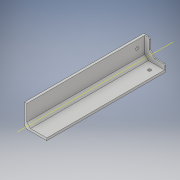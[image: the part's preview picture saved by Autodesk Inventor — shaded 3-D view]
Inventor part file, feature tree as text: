
AUTODESK INVENTOR PART (.ipt)
format: ipt  version: 2018 (Build 220112000, 112)  size: 189,440 bytes
history: native  units: in
note: dims shown in document units (in); Inventor stores cm internally (conversion verified against a paired STEP export)
features: sketch x7, extrude x3, hole x3, plane x1, fillet x1
ambient origin geometry x8: Origin, YZ Plane, XZ Plane, XY Plane, X Axis, Y Axis, Z Axis, Center Point
bodies: Solid1 (feature_tree)
feature tree (15):
  extrude  "Extrusion1"  Depth=0.75in
  extrude  "Extrusion2"  Depth=0.08in
  plane  "Work Plane1"
  extrude  "Extrusion4"  Depth=4.0in TaperAngle=0.0deg
  sketch  "Sketch6"  dims[d11=0.23in d15=0.23in d16=180.0deg]
  hole  "Hole1"  [1 undecoded]
  fillet  "Fillet1"  [1 undecoded]
  hole  "Hole2"  [1 undecoded]
  hole  "Hole3"  [1 undecoded]
  sketch  "Sketch1"  dims[d0=0.75in d1=0.75in]
  sketch  "Sketch2"  dims[d2=0.08in d3=0.08in]
  sketch  "Sketch5"  dims[d8=0.15in d9=4.0in d10=0.0in]
  sketch  "Sketch7"  dims[d18=90.0deg d20=45.0deg]
  sketch  "Sketch8"  dims[d21=0.4in d22=0.04in d23=0.0in]
  sketch  "Sketch9"  dims[d30=0.5in d37=0.05in d38=0.6in d39=180.0deg d40=0.25in d41=0.3in d42=0.25in d43=0.5in d44=0.2in d45=0.0in d46=0.25in d47=0.25in d48=0.75in d49=0.375in d50=0.25in d51=0.5635in d52=1.0in d53=0.8108in d54=0.05in d55=0.25in d56=0.3in d57=0.1in d58=0.75in d59=0.375in d60=0.25in d61=0.5635in d62=1.0in d63=0.8108in d64=0.25in d65=0.3in d66=0.1in d67=0.75in d68=0.375in d69=0.25in d70=0.5635in d71=1.0in d72=0.8108in d73=0.1in d74=0.6793in d75=0.4in]
note: 4 required parameter values undecoded (feature->parameter linkage not recoverable at this tier; creation-order binding heuristic only, values carry confidence <= 0.55)
